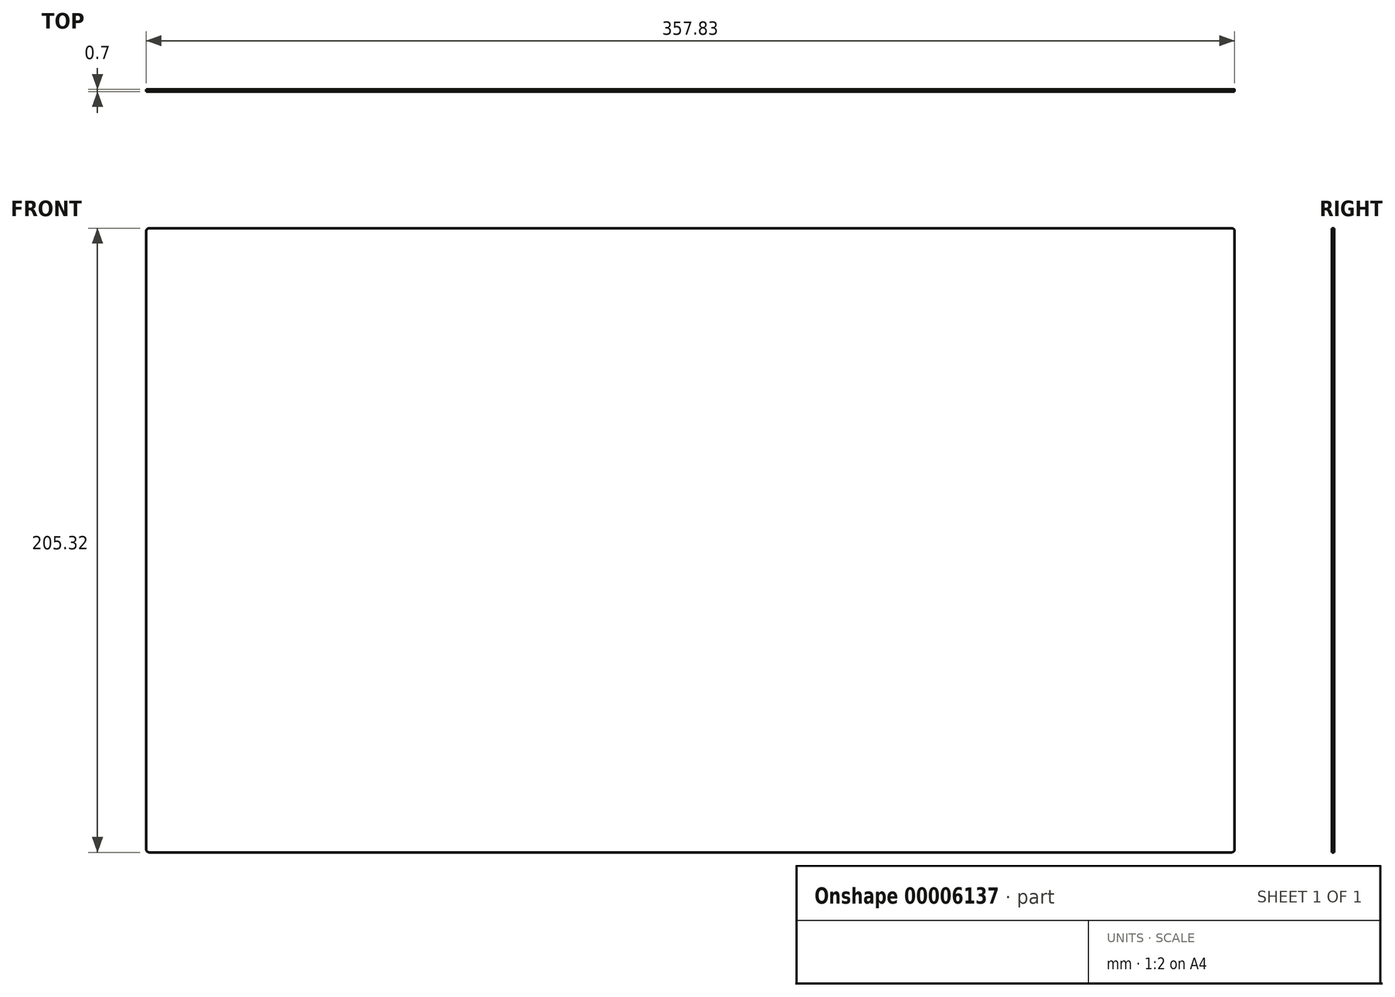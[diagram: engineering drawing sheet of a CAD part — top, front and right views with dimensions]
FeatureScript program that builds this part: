
annotation { "Feature Type Name" : "Feature", "Feature Type Description" : "" }
export const myFeature = defineFeature(function(context is Context, id is Id, definition is map)
    precondition{}
    {
        {
            var Q0;
            Q0=qCreatedBy(makeId("Front.planeOp"),FACE);
            var sketch = newSketch(context, id + "F0", { "sketchPlane" : qUnion([Q0])});
            skLineSegment(sketch, "E0.bottom", {"start": v(-177.91, -102.66) * mm, "end": v(177.92, -102.66) * mm});
            skLineSegment(sketch, "E0.top", {"start": v(-177.92, 102.66) * mm, "end": v(177.92, 102.66) * mm});
            skLineSegment(sketch, "E0.left", {"start": v(-178.91, -101.66) * mm, "end": v(-178.92, 101.66) * mm});
            skLineSegment(sketch, "E0.right", {"start": v(178.92, -101.66) * mm, "end": v(178.92, 101.66) * mm});
            skPoint(sketch, "E1.visualSharp", {"position": v(-178.91, 102.66) * mm});
            skArc(sketch, "E1.filletArc", {"start": v(-177.92, 102.66) * mm, "mid": v(-178.62, 102.37) * mm, "end": v(-178.92, 101.66) * mm});
            skPoint(sketch, "E2.visualSharp", {"position": v(178.92, 102.66) * mm});
            skArc(sketch, "E2.filletArc", {"start": v(178.92, 101.66) * mm, "mid": v(178.62, 102.37) * mm, "end": v(177.92, 102.66) * mm});
            skPoint(sketch, "E3.visualSharp", {"position": v(178.92, -102.66) * mm});
            skArc(sketch, "E3.filletArc", {"start": v(177.92, -102.66) * mm, "mid": v(178.62, -102.37) * mm, "end": v(178.92, -101.66) * mm});
            skPoint(sketch, "E4.visualSharp", {"position": v(-178.91, -102.66) * mm});
            skArc(sketch, "E4.filletArc", {"start": v(-178.91, -101.66) * mm, "mid": v(-178.62, -102.37) * mm, "end": v(-177.91, -102.66) * mm});
            skSolve(sketch);
        }
        {
            var Q0;
            Q0=makeQuery(id+"F0.imprint","IMPRINT",FACE,{"disambiguationData":[TD([[makeQuery(id+"F0.imprint","IMPRINT",EDGE,{"derivedFrom":sQuery(id+"F0.wireOp",EDGE,"E0.bottom")}),1.0]])]});
            extrude(context, id + "F1", {"entities" : qUnion([Q0]), "depth" : 0.7 * mm});
        }
    });
